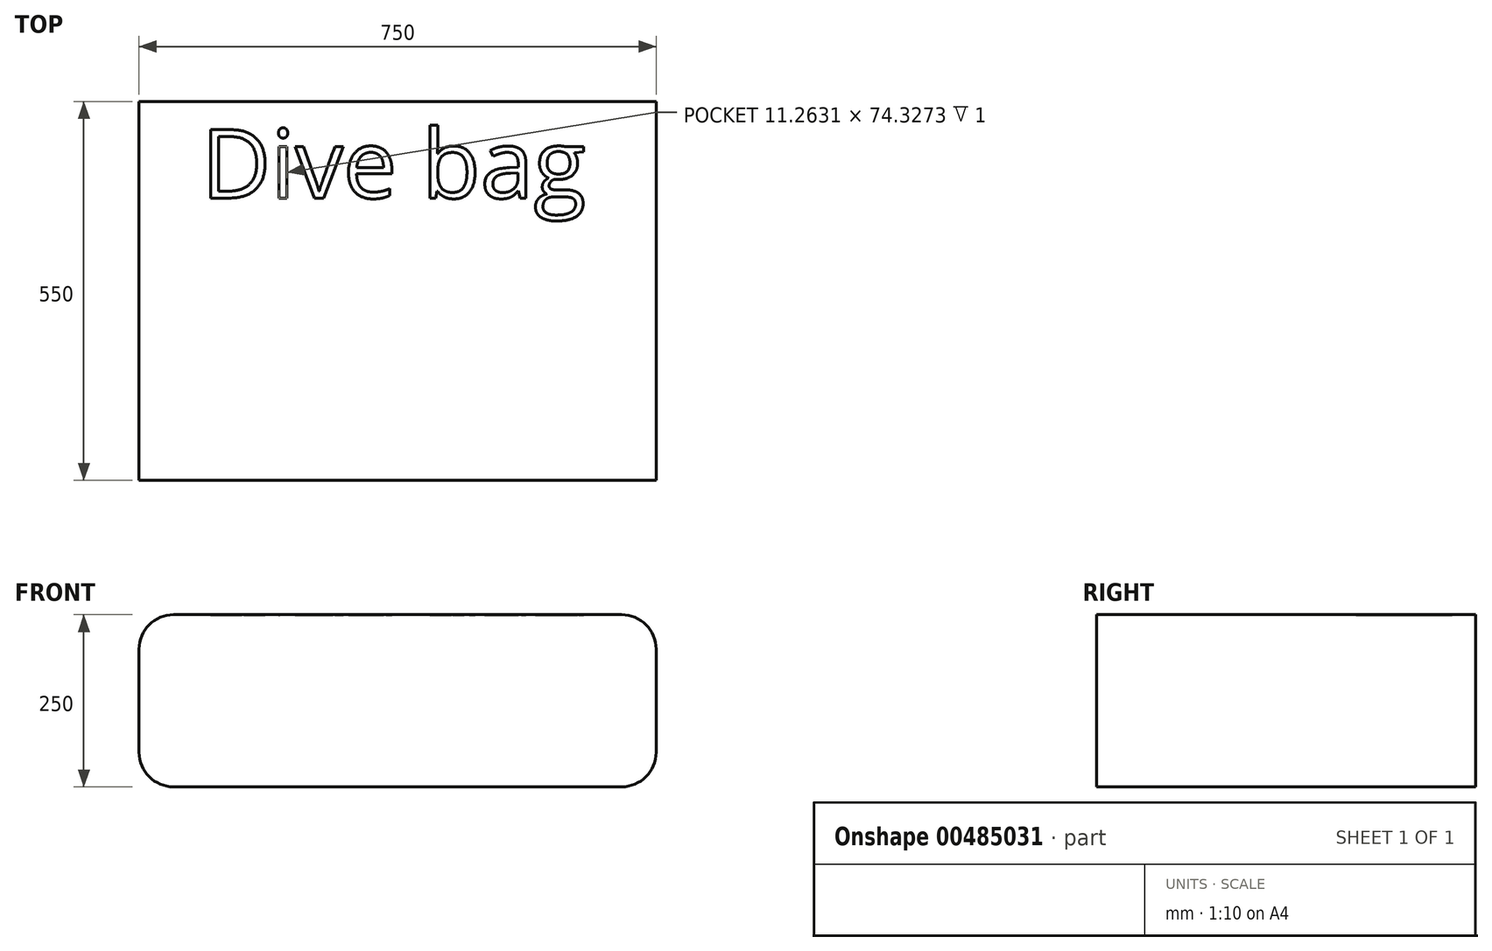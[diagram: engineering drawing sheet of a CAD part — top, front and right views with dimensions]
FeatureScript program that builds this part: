
annotation { "Feature Type Name" : "Feature", "Feature Type Description" : "" }
export const myFeature = defineFeature(function(context is Context, id is Id, definition is map)
    precondition{}
    {
        {
            var Q0;
            Q0=qCreatedBy(makeId("Front.planeOp"),FACE);
            var sketch = newSketch(context, id + "F0", { "sketchPlane" : qUnion([Q0])});
            skLineSegment(sketch, "E0.bottom", {"start": v(50, 0) * mm, "end": v(700, 0) * mm});
            skLineSegment(sketch, "E0.top", {"start": v(50, 250) * mm, "end": v(700, 250) * mm});
            skLineSegment(sketch, "E0.left", {"start": v(0, 50) * mm, "end": v(0, 200) * mm});
            skLineSegment(sketch, "E0.right", {"start": v(750, 50) * mm, "end": v(750, 200) * mm});
            skPoint(sketch, "E1.visualSharp", {"position": v(0, 250) * mm});
            skArc(sketch, "E1.filletArc", {"start": v(50, 250) * mm, "mid": v(14.64, 235.36) * mm, "end": v(0, 200) * mm});
            skPoint(sketch, "E2.visualSharp", {"position": v(0, 0) * mm});
            skArc(sketch, "E2.filletArc", {"start": v(0, 50) * mm, "mid": v(14.64, 14.64) * mm, "end": v(50, 0) * mm});
            skPoint(sketch, "E3.visualSharp", {"position": v(750, 0) * mm});
            skArc(sketch, "E3.filletArc", {"start": v(700, 0) * mm, "mid": v(735.36, 14.64) * mm, "end": v(750, 50) * mm});
            skPoint(sketch, "E4.visualSharp", {"position": v(750, 250) * mm});
            skArc(sketch, "E4.filletArc", {"start": v(750, 200) * mm, "mid": v(735.36, 235.36) * mm, "end": v(700, 250) * mm});
            skSolve(sketch);
        }
        {
            var Q0;
            Q0=makeQuery(id+"F0.imprint","IMPRINT",FACE,{"disambiguationData":[TD([[makeQuery(id+"F0.imprint","IMPRINT",EDGE,{"derivedFrom":sQuery(id+"F0.wireOp",EDGE,"E0.bottom")}),1.0]])]});
            extrude(context, id + "F1", {"entities" : qUnion([Q0]), "depth" : 550 * mm, "offsetDistance" : 25 * mm});
        }
        {
            var Q0;
            Q0=makeQuery(id+"F1.opExtrude","SWEPT_FACE",FACE,{"disambiguationData":[OSD([sQuery(id+"F0.wireOp",EDGE,"E0.top")])]});
            var sketch = newSketch(context, id + "F2", { "sketchPlane" : qUnion([Q0])});
            skText(sketch, "E5", { "text": "Dive bag", "fontName": "OpenSans-Regular.ttf"});
            const initialGuessF2  = {"E5": [0.09, -0.14, 1, 0, 0.1]};
            skSetInitialGuess(sketch, initialGuessF2);
            skSolve(sketch);
        }
        {
            var Q0;
            Q0 = qSketchRegion(id + "F2", true);
            extrude(context, id + "F3", {"entities" : qUnion([Q0]), "operationType" : NewBodyOperationType.REMOVE, "oppositeDirection" : true, "depth" : 1 * mm, "offsetDistance" : 25 * mm});
        }
    });
